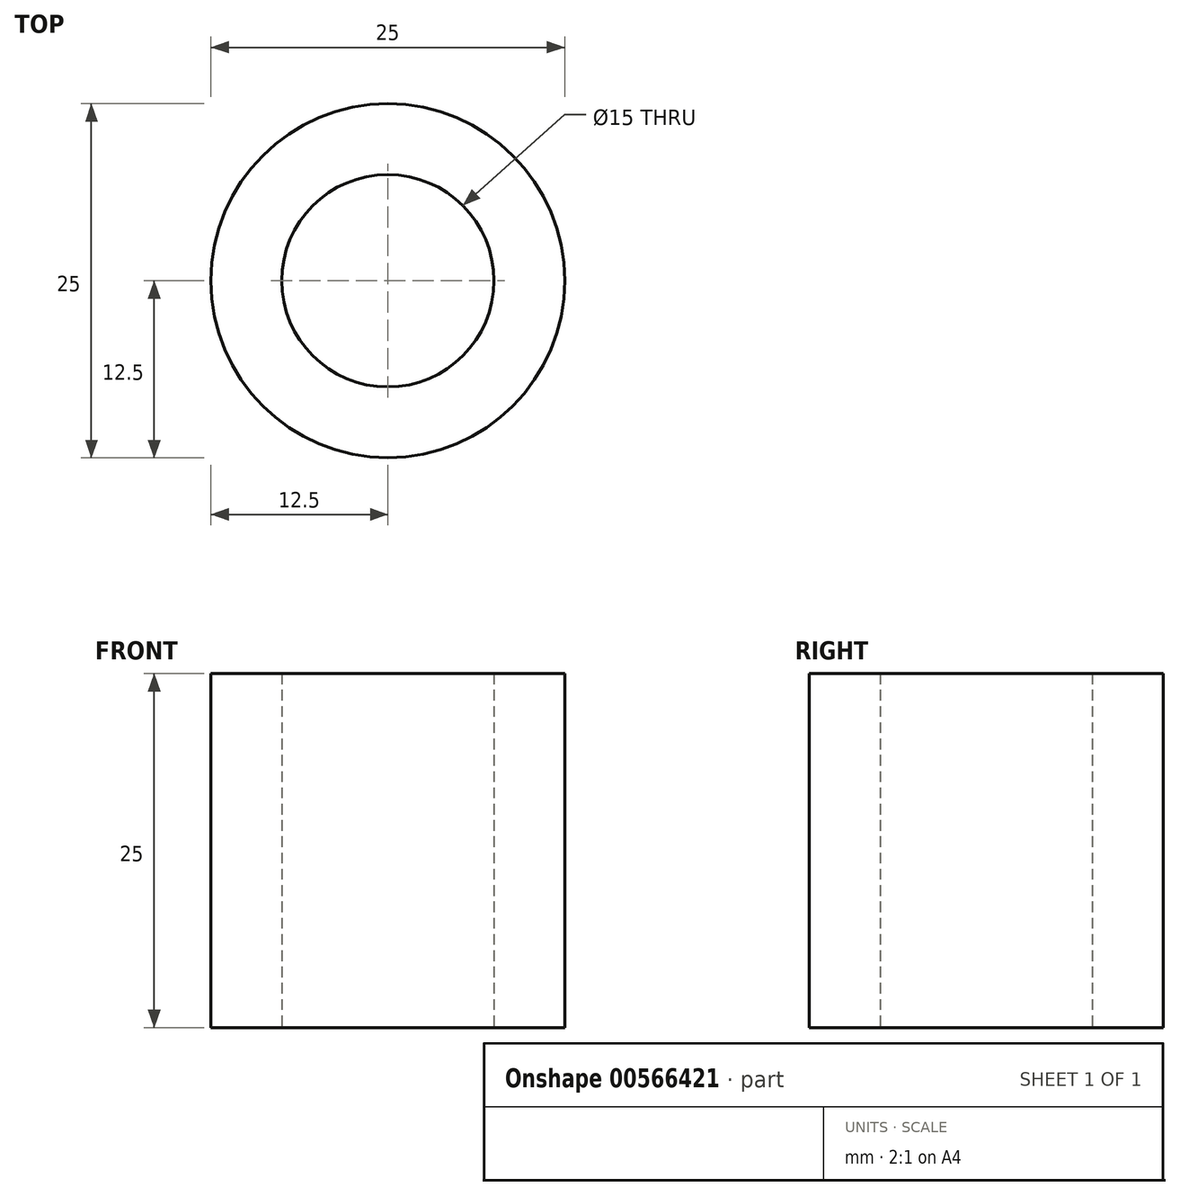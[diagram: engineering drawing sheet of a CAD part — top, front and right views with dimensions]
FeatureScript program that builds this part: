
annotation { "Feature Type Name" : "Feature", "Feature Type Description" : "" }
export const myFeature = defineFeature(function(context is Context, id is Id, definition is map)
    precondition{}
    {
        {
            var Q0;
            Q0=qCreatedBy(makeId("Top.planeOp"),FACE);
            var sketch = newSketch(context, id + "F0", { "sketchPlane" : qUnion([Q0])});
            skCircle(sketch, "E0", {"center": v(0, 0) * mm, "radius": 12.5 * mm});
            skCircle(sketch, "E1", {"center": v(0, 0) * mm, "radius": 7.5 * mm});
            skLineSegment(sketch, "E2", {"start": v(0, 0) * mm, "end": v(9.26, 8.4) * mm, "construction": true});
            skSolve(sketch);
        }
        {
            var Q0;
            Q0 = qSketchRegion(id + "F0", true);
            extrude(context, id + "F1", {"entities" : qUnion([Q0]), "depth" : 25 * mm, "offsetDistance" : 25 * mm});
        }
    });
